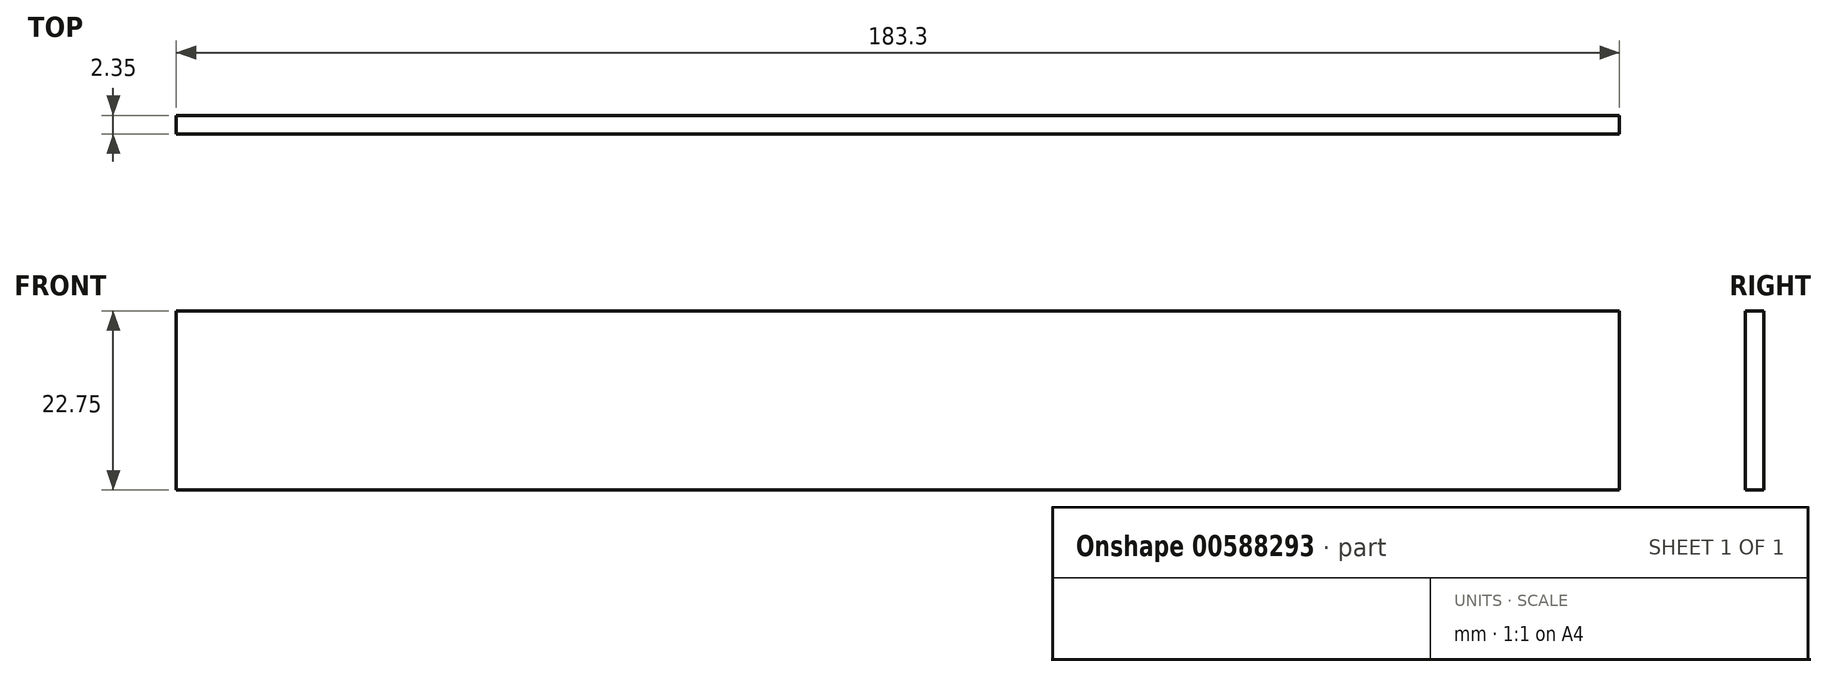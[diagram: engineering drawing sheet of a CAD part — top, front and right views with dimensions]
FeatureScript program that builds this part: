
annotation { "Feature Type Name" : "Feature", "Feature Type Description" : "" }
export const myFeature = defineFeature(function(context is Context, id is Id, definition is map)
    precondition{}
    {
        {
            var Q0;
            Q0=qCreatedBy(makeId("Front.planeOp"),FACE);
            var sketch = newSketch(context, id + "F0", { "sketchPlane" : qUnion([Q0])});
            skLineSegment(sketch, "E0.bottom", {"start": v(-135.74, 22.75) * mm, "end": v(47.56, 22.75) * mm});
            skLineSegment(sketch, "E0.top", {"start": v(-135.74, 0) * mm, "end": v(47.56, 0) * mm});
            skLineSegment(sketch, "E0.left", {"start": v(-135.74, 22.75) * mm, "end": v(-135.74, 0) * mm});
            skLineSegment(sketch, "E0.right", {"start": v(47.56, 22.75) * mm, "end": v(47.56, 0) * mm});
            skSolve(sketch);
        }
        {
            var Q0;
            Q0=makeQuery(id+"F0.imprint","IMPRINT",FACE,{"disambiguationData":[TD([[makeQuery(id+"F0.imprint","IMPRINT",EDGE,{"derivedFrom":sQuery(id+"F0.wireOp",EDGE,"E0.bottom")}),-1.0]])]});
            extrude(context, id + "F1", {"entities" : qUnion([Q0]), "depth" : 2.35 * mm, "offsetDistance" : 25 * mm});
        }
    });
